# Revit family: 1368xxx Cabin Semi Flush (UL)
name_source: partatom
category: Lighting Fixtures
revit_build: Autodesk Revit 2018 (Build: 20170223_1515(x64)
units: mm (PartAtom-declared; Revit-internal decimal feet)

## family parameters
Always vertical = Yes
Cut with Voids When Loaded = No
Host = Ceiling
Light Source = No
OmniClass Number = 23.80.70.11
OmniClass Title = Luminaries for Internal Lighting
Part Type = Normal
Room Calculation Point = No
Round Connector Dimension = Use Diameter
Shared = No

## types (6) — shared parameters
ADA compliant = Yes
Apparent Load = 0 VA
Dimmable = Yes
Dimming Method = Lamp Dependent
Driver Included = Not Applicable
Driver Required = No
Efficacy (lm/w) = Lamp Dependent
Electrical Class = 1
Lamp = Incandescent
Light Source Fixed = No
Location / IP Rating = Wet
Main Material = Metal - Zinc
Manufacturer URL - Europe and Rest of World = www.astrolighting.com
Manufacturer URL - North America = us.astrolighting.com
Power (Watts) = Lamp Dependent
Product CCT = Lamp Dependent
Product CRI = Lamp Dependent
Product Dimensions (MM) = 283x118x118
Product Location = Exterior
Product Name = Cabin Semi Flush
Product URL = https://us.astrolighting.com
Product Weight (KG) = 2 mm  [stored 0.00656168 ft]

## per-type parameters (varying)
| type | Main Finish | Product SKU |
| Astro Cabin Semi Flush Antique Brass | Antique Brass | 1368019 |
| Astro Cabin Semi Flush Polished Nickel | Polished Nickel | 1368020 |
| Astro Cabin Semi Flush Bronze | Bronze | 1368021 |
| Astro Cabin Semi Flush Frosted Antique Brass | Antique Brass | 1368013 |
| Astro Cabin Semi Flush Frosted Polished Nickel | Polished Nickel | 1368014 |
| Astro Cabin Semi Flush Frosted Bronze | Bronze | 1368015 |

note: [stored X ft] marks values corroborated as IEEE doubles in the binary element streams (Revit-internal decimal feet)

## geometry (parser evidence)
native form markers: Sweep x2
no freeform markers — native parametric forms only
